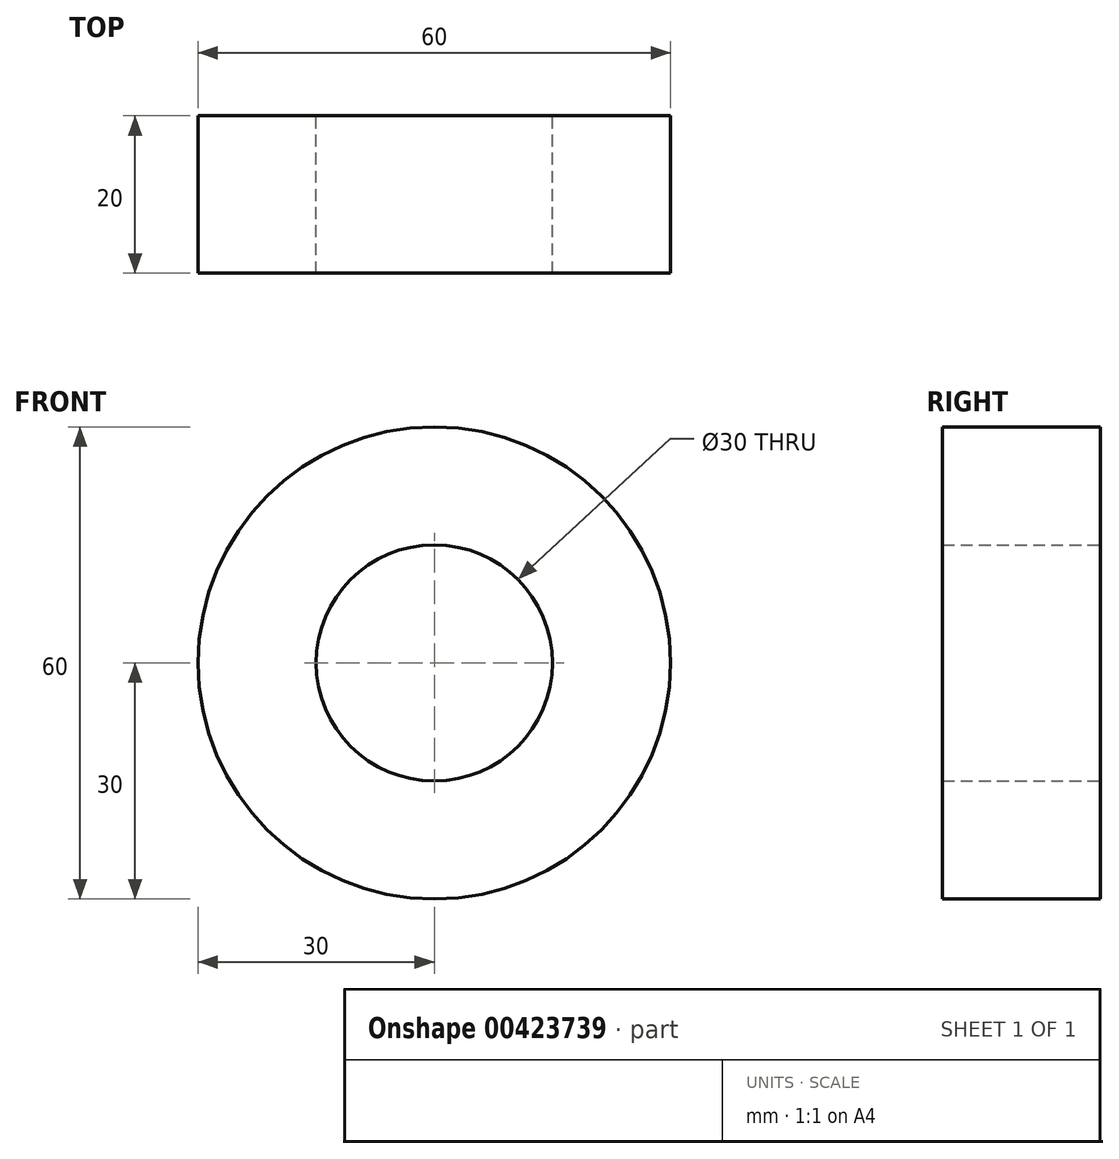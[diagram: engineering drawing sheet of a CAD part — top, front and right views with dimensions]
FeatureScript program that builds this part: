
annotation { "Feature Type Name" : "Feature", "Feature Type Description" : "" }
export const myFeature = defineFeature(function(context is Context, id is Id, definition is map)
    precondition{}
    {
        {
            var Q0;
            Q0=qCreatedBy(makeId("Front.planeOp"),FACE);
            var sketch = newSketch(context, id + "F0", { "sketchPlane" : qUnion([Q0])});
            skCircle(sketch, "E0", {"center": v(0, 0) * mm, "radius": 30 * mm});
            skCircle(sketch, "E1", {"center": v(0, 0) * mm, "radius": 15 * mm});
            skSolve(sketch);
        }
        {
            var Q0;
            Q0 = qSketchRegion(id + "F0", true);
            extrude(context, id + "F1", {"entities" : qUnion([Q0]), "endBound" : BoundingType.SYMMETRIC, "depth" : 20 * mm});
        }
    });
